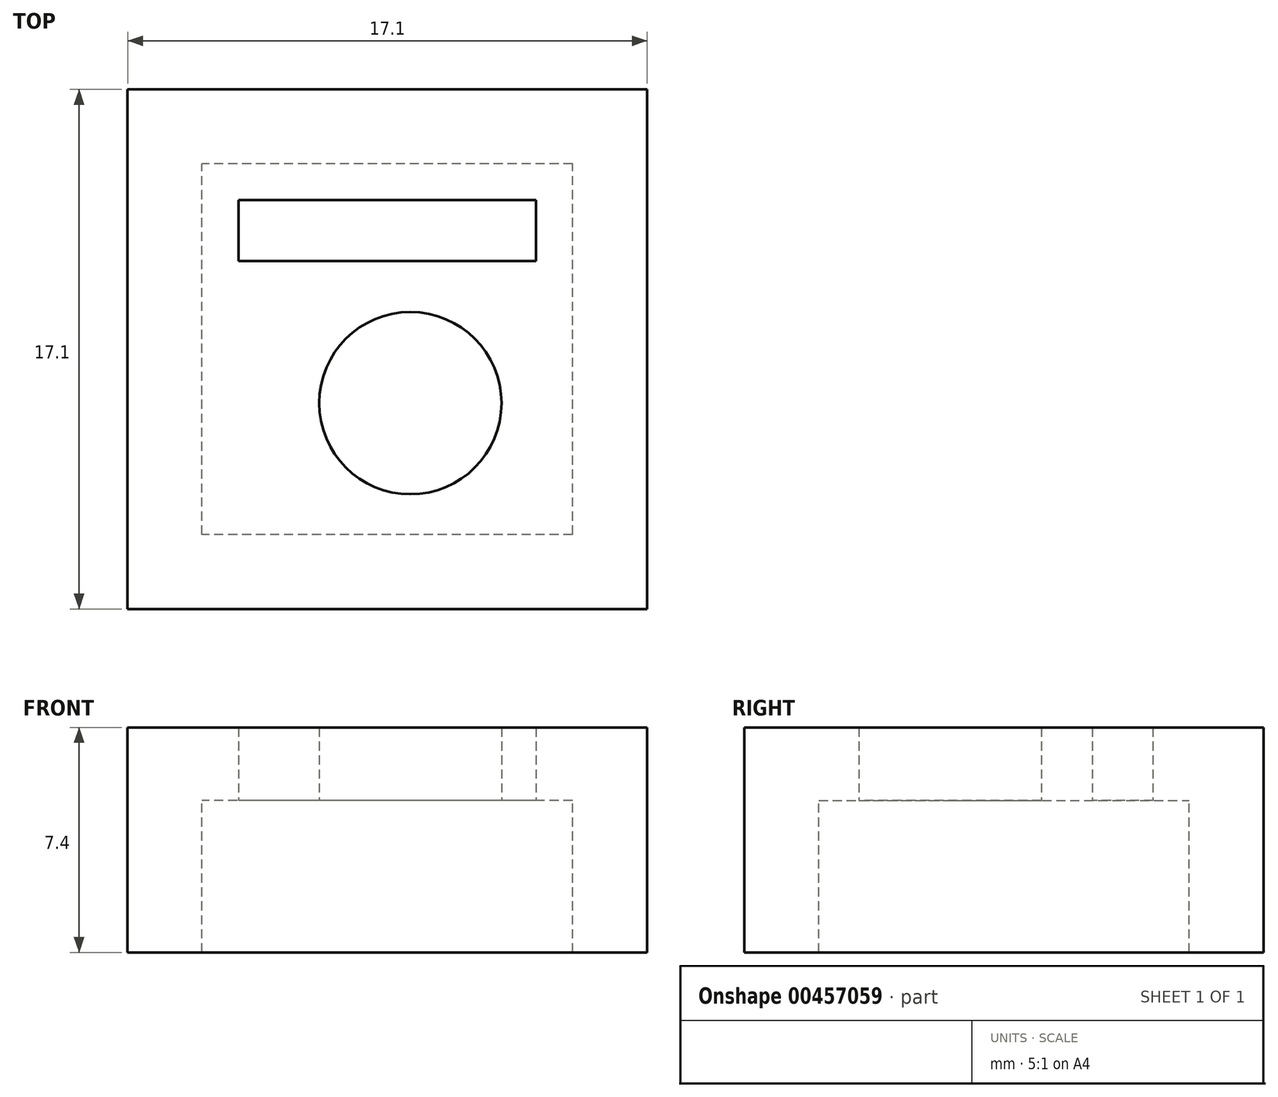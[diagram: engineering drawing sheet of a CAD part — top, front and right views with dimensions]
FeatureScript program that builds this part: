
annotation { "Feature Type Name" : "Feature", "Feature Type Description" : "" }
export const myFeature = defineFeature(function(context is Context, id is Id, definition is map)
    precondition{}
    {
        {
            var Q0;
            Q0=qCreatedBy(makeId("Top.planeOp"),FACE);
            var sketch = newSketch(context, id + "F0", { "sketchPlane" : qUnion([Q0])});
            skLineSegment(sketch, "E0.bottom", {"start": v(8.88, -7) * mm, "end": v(-8.22, -7) * mm});
            skLineSegment(sketch, "E0.top", {"start": v(8.88, 10.1) * mm, "end": v(-8.22, 10.1) * mm});
            skLineSegment(sketch, "E0.left", {"start": v(8.88, -7) * mm, "end": v(8.88, 10.1) * mm});
            skLineSegment(sketch, "E0.right", {"start": v(-8.22, -7) * mm, "end": v(-8.22, 10.1) * mm});
            skLineSegment(sketch, "E1", {"start": v(8.88, -7) * mm, "end": v(8.88, 1.55) * mm});
            skLineSegment(sketch, "E2", {"start": v(8.88, 1.55) * mm, "end": v(0.33, 1.55) * mm});
            skLineSegment(sketch, "E3", {"start": v(8.88, -7) * mm, "end": v(8.88, -4.5) * mm});
            skLineSegment(sketch, "E4", {"start": v(8.88, 10.1) * mm, "end": v(8.88, 7.6) * mm});
            skLineSegment(sketch, "E5", {"start": v(8.88, 7.6) * mm, "end": v(8.88, -4.5) * mm});
            skLineSegment(sketch, "E6", {"start": v(0.33, 1.55) * mm, "end": v(0.33, 5.45) * mm});
            skLineSegment(sketch, "E7.bottom", {"start": v(5.23, 6.45) * mm, "end": v(-4.57, 6.45) * mm});
            skLineSegment(sketch, "E7.top", {"start": v(5.23, 4.45) * mm, "end": v(-4.57, 4.45) * mm});
            skLineSegment(sketch, "E7.left", {"start": v(5.23, 6.45) * mm, "end": v(5.23, 4.45) * mm});
            skLineSegment(sketch, "E7.right", {"start": v(-4.57, 6.45) * mm, "end": v(-4.57, 4.45) * mm});
            skPoint(sketch, "E7.middle", {"position": v(0.33, 5.45) * mm});
            skLineSegment(sketch, "E8", {"start": v(0.33, 1.55) * mm, "end": v(-8.22, 1.55) * mm});
            skLineSegment(sketch, "E9", {"start": v(8.88, 1.55) * mm, "end": v(8.88, 10.1) * mm});
            skCircle(sketch, "E10", {"center": v(1.09, -0.22) * mm, "radius": 3 * mm});
            skLineSegment(sketch, "E11.bottom", {"start": v(6.43, -4.55) * mm, "end": v(-5.77, -4.55) * mm});
            skLineSegment(sketch, "E11.top", {"start": v(6.43, 7.65) * mm, "end": v(-5.77, 7.65) * mm});
            skLineSegment(sketch, "E11.left", {"start": v(6.43, -4.55) * mm, "end": v(6.43, 7.65) * mm});
            skLineSegment(sketch, "E11.right", {"start": v(-5.77, -4.55) * mm, "end": v(-5.77, 7.65) * mm});
            skPoint(sketch, "E11.middle", {"position": v(0.33, 1.55) * mm});
            skCircle(sketch, "E12", {"center": v(1.09, -0.22) * mm, "radius": 5.2 * mm});
            skSolve(sketch);
        }
        {
            var Q0;
            {var subQ17=sQuery(id+"F0.wireOp",EDGE,"E0.bottom");Q0=makeQuery(id+"F0.imprint","IMPRINT",FACE,{"disambiguationData":[TD([[makeQuery(id+"F0.imprint","IMPRINT",EDGE,{"derivedFrom":subQ17}),-1.0]])]});}
            var Q1;
            {var subQ9=sQuery(id+"F0.wireOp",EDGE,"E0.top");Q1=makeQuery(id+"F0.imprint","IMPRINT",FACE,{"disambiguationData":[TD([[makeQuery(id+"F0.imprint","IMPRINT",EDGE,{"derivedFrom":subQ9}),1.0]])]});}
            var Q2;
            {var subQ0=sQuery(id+"F0.wireOp",EDGE,"E12");var subQ1=sQuery(id+"F0.wireOp",EDGE,"E11.bottom");var subQ2=makeQuery(id+"F0.imprint","INTERSECT",VERTEX,{"disambiguationData":[OD(0.0)],"derivedFrom":[subQ1,subQ0]});Q2=makeQuery(id+"F0.imprint","IMPRINT",FACE,{"disambiguationData":[TD([[makeQuery(id+"F0.imprint","IMPRINT",EDGE,{"disambiguationData":[TD([[subQ2,-1.0]])],"derivedFrom":subQ1}),1.0]])]});}
            extrude(context, id + "F1", {"entities" : qUnion([Q0, Q1, Q2]), "depth" : -5 * mm});
        }
        {
            var Q0;
            {var subQ9=sQuery(id+"F0.wireOp",EDGE,"E0.top");Q0=makeQuery(id+"F0.imprint","IMPRINT",FACE,{"disambiguationData":[TD([[makeQuery(id+"F0.imprint","IMPRINT",EDGE,{"derivedFrom":subQ9}),1.0]])]});}
            var Q1;
            Q1=makeQuery(id+"F0.imprint","IMPRINT",FACE,{"disambiguationData":[TD([[makeQuery(id+"F0.imprint","IMPRINT",EDGE,{"derivedFrom":sQuery(id+"F0.wireOp",EDGE,"E7.bottom")}),-1.0]])]});
            var Q2;
            {var subQ0=sQuery(id+"F0.wireOp",EDGE,"E10");var subQ1=sQuery(id+"F0.wireOp",EDGE,"E6");var subQ2=makeQuery(id+"F0.imprint","INTERSECT",VERTEX,{"derivedFrom":[subQ1,subQ0]});Q2=makeQuery(id+"F0.imprint","IMPRINT",FACE,{"disambiguationData":[TD([[makeQuery(id+"F0.imprint","IMPRINT",EDGE,{"disambiguationData":[TD([[subQ2,-1.0]])],"derivedFrom":subQ1}),1.0]])]});}
            var Q3;
            {var subQ1=sQuery(id+"F0.wireOp",EDGE,"E2");var subQ5=sQuery(id+"F0.wireOp",EDGE,"E12");var subQ6=makeQuery(id+"F0.imprint","INTERSECT",VERTEX,{"derivedFrom":[subQ1,subQ5]});Q3=makeQuery(id+"F0.imprint","IMPRINT",FACE,{"disambiguationData":[TD([[makeQuery(id+"F0.imprint","IMPRINT",EDGE,{"disambiguationData":[TD([[subQ6,-1.0]])],"derivedFrom":subQ1}),-1.0]])]});}
            var Q4;
            {var subQ0=sQuery(id+"F0.wireOp",EDGE,"E12");var subQ7=sQuery(id+"F0.wireOp",EDGE,"E2");var subQ10=makeQuery(id+"F0.imprint","INTERSECT",VERTEX,{"derivedFrom":[subQ7,subQ0]});Q4=makeQuery(id+"F0.imprint","IMPRINT",FACE,{"disambiguationData":[TD([[makeQuery(id+"F0.imprint","IMPRINT",EDGE,{"disambiguationData":[TD([[subQ10,-1.0]])],"derivedFrom":subQ7}),1.0]])]});}
            var Q5;
            {var subQ0=sQuery(id+"F0.wireOp",EDGE,"E12");var subQ1=sQuery(id+"F0.wireOp",EDGE,"E8");var subQ2=makeQuery(id+"F0.imprint","INTERSECT",VERTEX,{"derivedFrom":[subQ1,subQ0]});Q5=makeQuery(id+"F0.imprint","IMPRINT",FACE,{"disambiguationData":[TD([[makeQuery(id+"F0.imprint","IMPRINT",EDGE,{"disambiguationData":[TD([[subQ2,-1.0]])],"derivedFrom":subQ1}),1.0]])]});}
            var Q6;
            {var subQ14=sQuery(id+"F0.wireOp",EDGE,"E0.bottom");Q6=makeQuery(id+"F0.imprint","IMPRINT",FACE,{"disambiguationData":[TD([[makeQuery(id+"F0.imprint","IMPRINT",EDGE,{"derivedFrom":subQ14}),-1.0]])]});}
            var Q7;
            {var subQ0=sQuery(id+"F0.wireOp",EDGE,"E12");var subQ1=sQuery(id+"F0.wireOp",EDGE,"E11.bottom");var subQ2=makeQuery(id+"F0.imprint","INTERSECT",VERTEX,{"disambiguationData":[OD(0.0)],"derivedFrom":[subQ1,subQ0]});Q7=makeQuery(id+"F0.imprint","IMPRINT",FACE,{"disambiguationData":[TD([[makeQuery(id+"F0.imprint","IMPRINT",EDGE,{"disambiguationData":[TD([[subQ2,-1.0]])],"derivedFrom":subQ1}),1.0]])]});}
            var Q8;
            {var subQ0=sQuery(id+"F0.wireOp",EDGE,"E11.left");var subQ1=sQuery(id+"F0.wireOp",EDGE,"E2");var subQ2=makeQuery(id+"F0.imprint","INTERSECT",VERTEX,{"derivedFrom":[subQ1,subQ0]});Q8=makeQuery(id+"F0.imprint","IMPRINT",FACE,{"disambiguationData":[TD([[makeQuery(id+"F0.imprint","IMPRINT",EDGE,{"disambiguationData":[TD([[subQ2,-1.0]])],"derivedFrom":subQ1}),1.0]])]});}
            extrude(context, id + "F2", {"entities" : qUnion([Q0, Q1, Q2, Q3, Q4, Q5, Q6, Q7, Q8]), "operationType" : NewBodyOperationType.ADD, "depth" : 2.4 * mm});
        }
    });
